# Revit family: Faucet-Wall_Mount-Kitchen-KOHLER-HiRise-K-7322
name_source: partatom
category: Plumbing Fixtures
revit_build: Autodesk Revit 2015 (Build: 20140606_1530(x64)
units: mm (PartAtom-declared; Revit-internal decimal feet)

## types (2) — shared parameters
ADA Compliant = No
Assembly Code = D2010
CW Connection = Yes
Cold Water Inlet = Cold Water Inlet
Date Modified = 02/04/2019
Default Elevation = 36"
Description = Single-hole wall-mount pot filler kitchen sink faucet with 24 inch extended spout and lever handle
Drain Included = No
Faucet Hole Spacing = 0"
Flow Rate = 7 GPM
HW Connection = No
Handle Clearance = 2 3/4"
Height = 7 3/8"
Hot Water Inlet = Hot Water Inlet
Length = 13 1/2"
Manufacturer = KOHLER Co.
MasterFormat 1995 = 15410
MasterFormat 2004 = 22.41.39
Material = Stainless Steel Construction
Pressure = 60.00 psi
Product Documentation Link = https://www.us.kohler.com
Product Name = HiRise
Product Page URL = http://www.us.kohler.com
Spout Reach = 22"
URL = https://www.us.kohler.com
Vent Connection = No
Waste Connection = No
Waste Water Outlet = Waste Water Outlet
WaterSense Certified = No
Width = 2 7/8"

## per-type parameters (varying)
| type | Finish | Model | Type |
| S-Polished Stainless | Kohler-Metal-S-Polished_Stainless | K-7322-4-S | 1 |
| BS-Brushed Stainless | Kohler-Metal-BS-Brushed_Stainless | K-7322-4-BS | 2 |

## geometry (parser evidence)
native form markers: Sweep x5
no freeform markers — native parametric forms only
